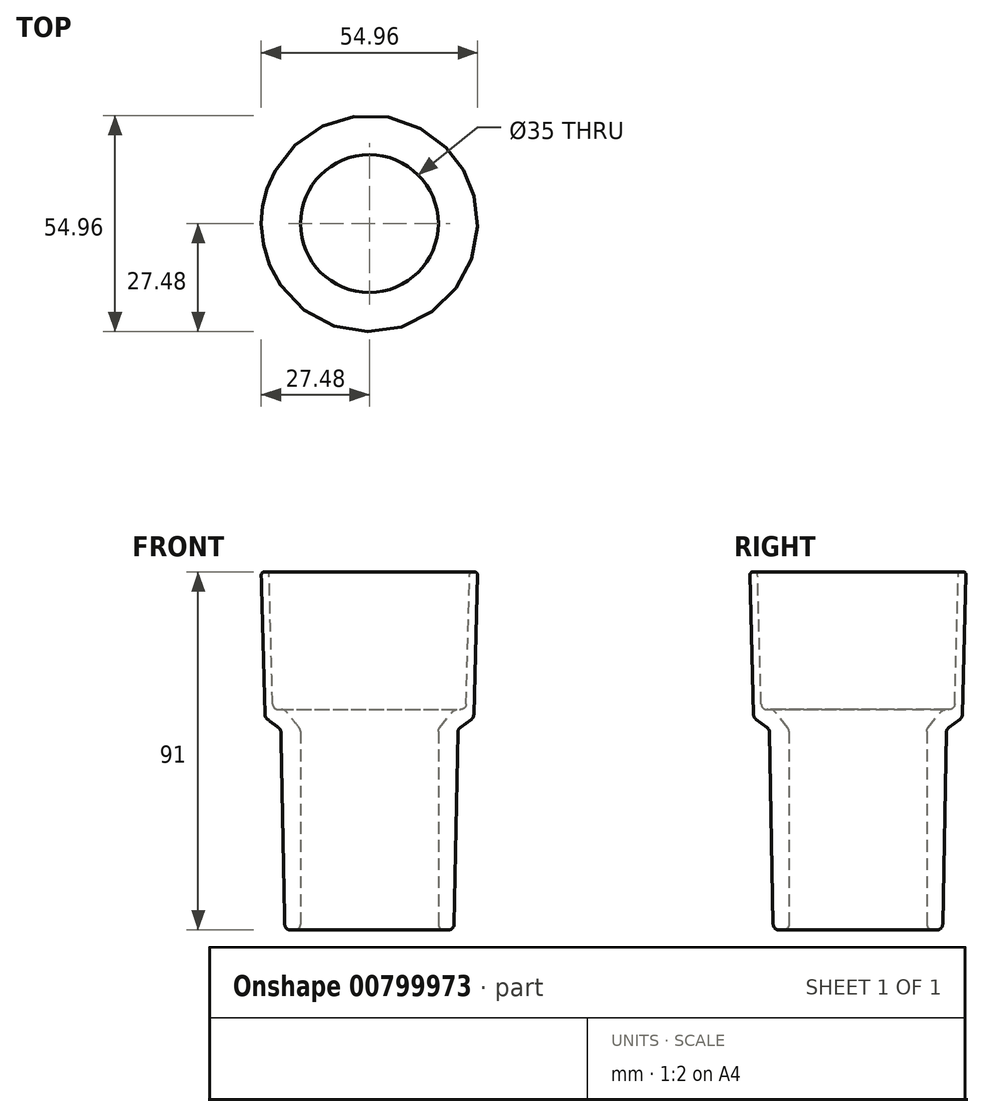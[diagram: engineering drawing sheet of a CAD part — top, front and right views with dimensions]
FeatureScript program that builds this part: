
annotation { "Feature Type Name" : "Feature", "Feature Type Description" : "" }
export const myFeature = defineFeature(function(context is Context, id is Id, definition is map)
    precondition{}
    {
        {
            var Q0;
            Q0=qCreatedBy(makeId("Front.planeOp"),FACE);
            var sketch = newSketch(context, id + "F0", { "sketchPlane" : qUnion([Q0])});
            skLineSegment(sketch, "E0", {"start": v(0, 0) * mm, "end": v(27.5, 0) * mm, "construction": true});
            skLineSegment(sketch, "E1", {"start": v(27.5, 0) * mm, "end": v(27.5, 91) * mm, "construction": true});
            skLineSegment(sketch, "E2", {"start": v(27.5, 54) * mm, "end": v(0, 54) * mm, "construction": true});
            skLineSegment(sketch, "E3", {"start": v(27.5, 51) * mm, "end": v(0, 51) * mm, "construction": true});
            skLineSegment(sketch, "E4", {"start": v(27.48, 90.18) * mm, "end": v(26.52, 54.72) * mm});
            skLineSegment(sketch, "E5", {"start": v(25.92, 53.57) * mm, "end": v(23.09, 51.44) * mm});
            skLineSegment(sketch, "E6", {"start": v(22.49, 50.27) * mm, "end": v(21.53, 1.47) * mm});
            skLineSegment(sketch, "E7", {"start": v(20.03, 0) * mm, "end": v(19, 0) * mm});
            skLineSegment(sketch, "E8", {"start": v(17.5, 1.5) * mm, "end": v(17.5, 50.47) * mm});
            skLineSegment(sketch, "E9", {"start": v(26.28, 91) * mm, "end": v(26.68, 91) * mm});
            skLineSegment(sketch, "E10", {"start": v(27.5, 56) * mm, "end": v(0, 56) * mm, "construction": true});
            skLineSegment(sketch, "E11", {"start": v(25.48, 90.22) * mm, "end": v(24.6, 57.46) * mm});
            skLineSegment(sketch, "E12", {"start": v(23.1, 56) * mm, "end": v(22.27, 56) * mm});
            skLineSegment(sketch, "E13", {"start": v(21.1, 55.44) * mm, "end": v(17.83, 51.41) * mm});
            skPoint(sketch, "E14.visualSharp", {"position": v(24.55, 56) * mm});
            skArc(sketch, "E14.filletArc", {"start": v(23.1, 56) * mm, "mid": v(24.14, 56.43) * mm, "end": v(24.6, 57.46) * mm});
            skPoint(sketch, "E15.visualSharp", {"position": v(22.5, 51) * mm});
            skArc(sketch, "E15.filletArc", {"start": v(23.09, 51.44) * mm, "mid": v(22.65, 50.92) * mm, "end": v(22.49, 50.27) * mm});
            skPoint(sketch, "E16.visualSharp", {"position": v(26.5, 54) * mm});
            skArc(sketch, "E16.filletArc", {"start": v(25.92, 53.57) * mm, "mid": v(26.35, 54.08) * mm, "end": v(26.52, 54.72) * mm});
            skPoint(sketch, "E17.visualSharp", {"position": v(21.55, 56) * mm});
            skArc(sketch, "E17.filletArc", {"start": v(22.27, 56) * mm, "mid": v(21.62, 55.85) * mm, "end": v(21.1, 55.44) * mm});
            skPoint(sketch, "E18.visualSharp", {"position": v(17.5, 51) * mm});
            skArc(sketch, "E18.filletArc", {"start": v(17.83, 51.41) * mm, "mid": v(17.59, 50.97) * mm, "end": v(17.5, 50.47) * mm});
            skPoint(sketch, "E19.visualSharp", {"position": v(25.5, 91) * mm});
            skArc(sketch, "E19.filletArc", {"start": v(26.28, 91) * mm, "mid": v(25.72, 90.77) * mm, "end": v(25.48, 90.22) * mm});
            skPoint(sketch, "E20.visualSharp", {"position": v(27.5, 91) * mm});
            skArc(sketch, "E20.filletArc", {"start": v(27.48, 90.18) * mm, "mid": v(27.25, 90.76) * mm, "end": v(26.68, 91) * mm});
            skPoint(sketch, "E21.visualSharp", {"position": v(21.5, 0) * mm});
            skArc(sketch, "E21.filletArc", {"start": v(20.03, 0) * mm, "mid": v(21.08, 0.43) * mm, "end": v(21.53, 1.47) * mm});
            skPoint(sketch, "E22.visualSharp", {"position": v(17.5, 0) * mm});
            skArc(sketch, "E22.filletArc", {"start": v(17.5, 1.5) * mm, "mid": v(17.94, 0.44) * mm, "end": v(19, 0) * mm});
            skLineSegment(sketch, "E23", {"start": v(0, 0) * mm, "end": v(0, 93.18) * mm, "construction": true});
            skSolve(sketch);
        }
        {
            var Q0;
            Q0=makeQuery(id+"F0.imprint","IMPRINT",FACE,{"disambiguationData":[TD([[makeQuery(id+"F0.imprint","IMPRINT",EDGE,{"derivedFrom":sQuery(id+"F0.wireOp",EDGE,"E4")}),-1.0]])]});
            var Q1;
            Q1=sQuery(id+"F0.wireOp",EDGE,"E23");
            revolve(context, id + "F1", {"surfaceOperationType" : NewSurfaceOperationType.NEW, "entities" : qUnion([Q0]), "axis" : qUnion([Q1]), "revolveType" : RevolveType.FULL});
        }
    });
